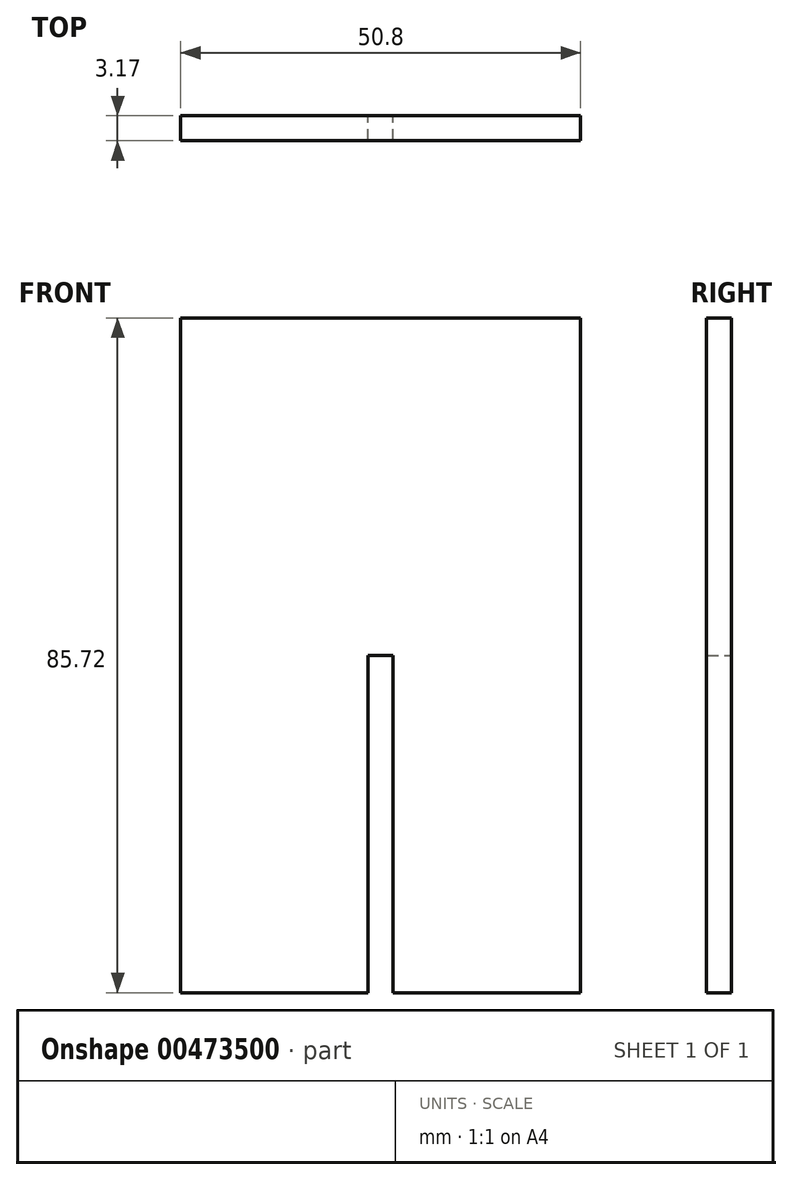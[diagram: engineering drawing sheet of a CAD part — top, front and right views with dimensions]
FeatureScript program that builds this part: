
annotation { "Feature Type Name" : "Feature", "Feature Type Description" : "" }
export const myFeature = defineFeature(function(context is Context, id is Id, definition is map)
    precondition{}
    {
        {
            var Q0;
            Q0=qCreatedBy(makeId("Front.planeOp"),FACE);
            var sketch = newSketch(context, id + "F0", { "sketchPlane" : qUnion([Q0])});
            skLineSegment(sketch, "E0.bottom", {"start": v(25.4, 42.86) * mm, "end": v(-25.4, 42.86) * mm});
            skLineSegment(sketch, "E0.top", {"start": v(25.4, -42.86) * mm, "end": v(1.59, -42.86) * mm});
            skLineSegment(sketch, "E0.left", {"start": v(25.4, 42.86) * mm, "end": v(25.4, -42.86) * mm});
            skLineSegment(sketch, "E0.right", {"start": v(-25.4, 42.86) * mm, "end": v(-25.4, -42.86) * mm});
            skPoint(sketch, "E0.middle", {"position": v(0, 0) * mm});
            skLineSegment(sketch, "E1", {"start": v(-25.4, -42.86) * mm, "end": v(-1.59, -42.86) * mm});
            skLineSegment(sketch, "E2", {"start": v(-1.59, -42.86) * mm, "end": v(-1.59, 0) * mm});
            skLineSegment(sketch, "E3", {"start": v(-1.59, 0) * mm, "end": v(1.59, 0) * mm});
            skLineSegment(sketch, "E4", {"start": v(1.59, 0) * mm, "end": v(1.59, -42.86) * mm});
            skLineSegment(sketch, "E5.trimOffspring", {"start": v(-1.59, -42.86) * mm, "end": v(-25.4, -42.86) * mm});
            skSolve(sketch);
        }
        {
            var Q0;
            Q0 = qSketchRegion(id + "F0", true);
            extrude(context, id + "F1", {"entities" : qUnion([Q0]), "depth" : 3.17 * mm});
        }
    });
